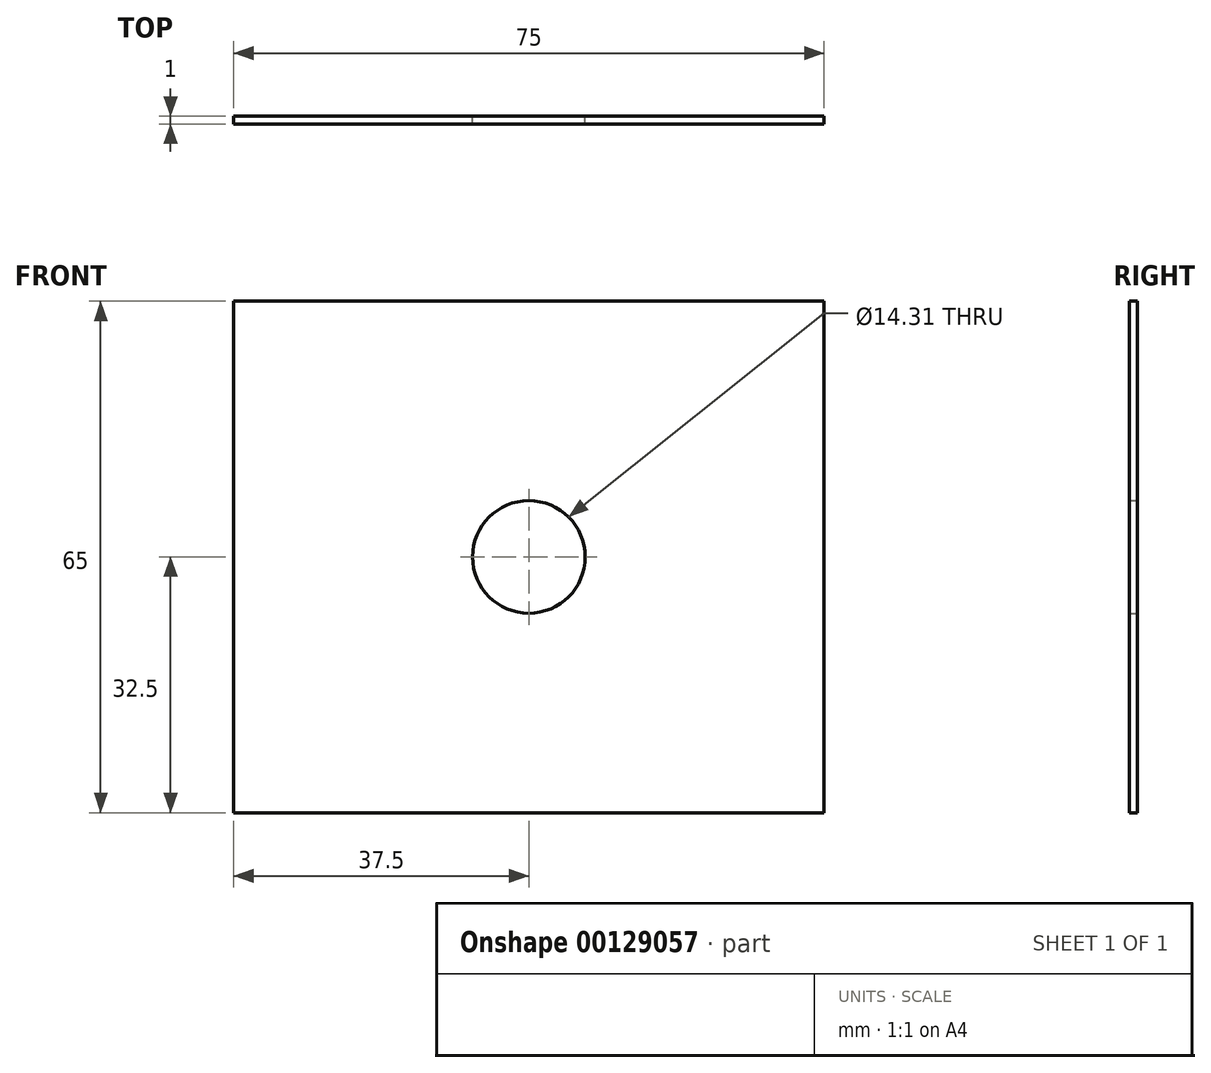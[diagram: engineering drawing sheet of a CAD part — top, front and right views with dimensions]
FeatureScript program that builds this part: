
annotation { "Feature Type Name" : "Feature", "Feature Type Description" : "" }
export const myFeature = defineFeature(function(context is Context, id is Id, definition is map)
    precondition{}
    {
        {
            var Q0;
            Q0=qCreatedBy(makeId("Front.planeOp"),FACE);
            var sketch = newSketch(context, id + "F0", { "sketchPlane" : qUnion([Q0])});
            skLineSegment(sketch, "E0.bottom", {"start": v(0, 0) * mm, "end": v(75, 0) * mm});
            skLineSegment(sketch, "E0.top", {"start": v(0, 65) * mm, "end": v(75, 65) * mm});
            skLineSegment(sketch, "E0.left", {"start": v(0, 0) * mm, "end": v(0, 65) * mm});
            skLineSegment(sketch, "E0.right", {"start": v(75, 0) * mm, "end": v(75, 65) * mm});
            skLineSegment(sketch, "E1", {"start": v(0, 0) * mm, "end": v(37.5, 0) * mm});
            skLineSegment(sketch, "E2", {"start": v(37.5, 65) * mm, "end": v(37.5, 0) * mm});
            skLineSegment(sketch, "E3", {"start": v(0, 0) * mm, "end": v(0, 32.5) * mm});
            skLineSegment(sketch, "E4", {"start": v(75, 0) * mm, "end": v(75, 32.5) * mm});
            skLineSegment(sketch, "E5", {"start": v(0, 32.5) * mm, "end": v(75, 32.5) * mm});
            skCircle(sketch, "E6", {"center": v(37.5, 32.5) * mm, "radius": 7.15 * mm});
            skSolve(sketch);
        }
        {
            var Q0;
            Q0 = qSketchRegion(id + "F0", true);
            extrude(context, id + "F1", {"entities" : qUnion([Q0]), "depth" : 1 * mm});
        }
    });
